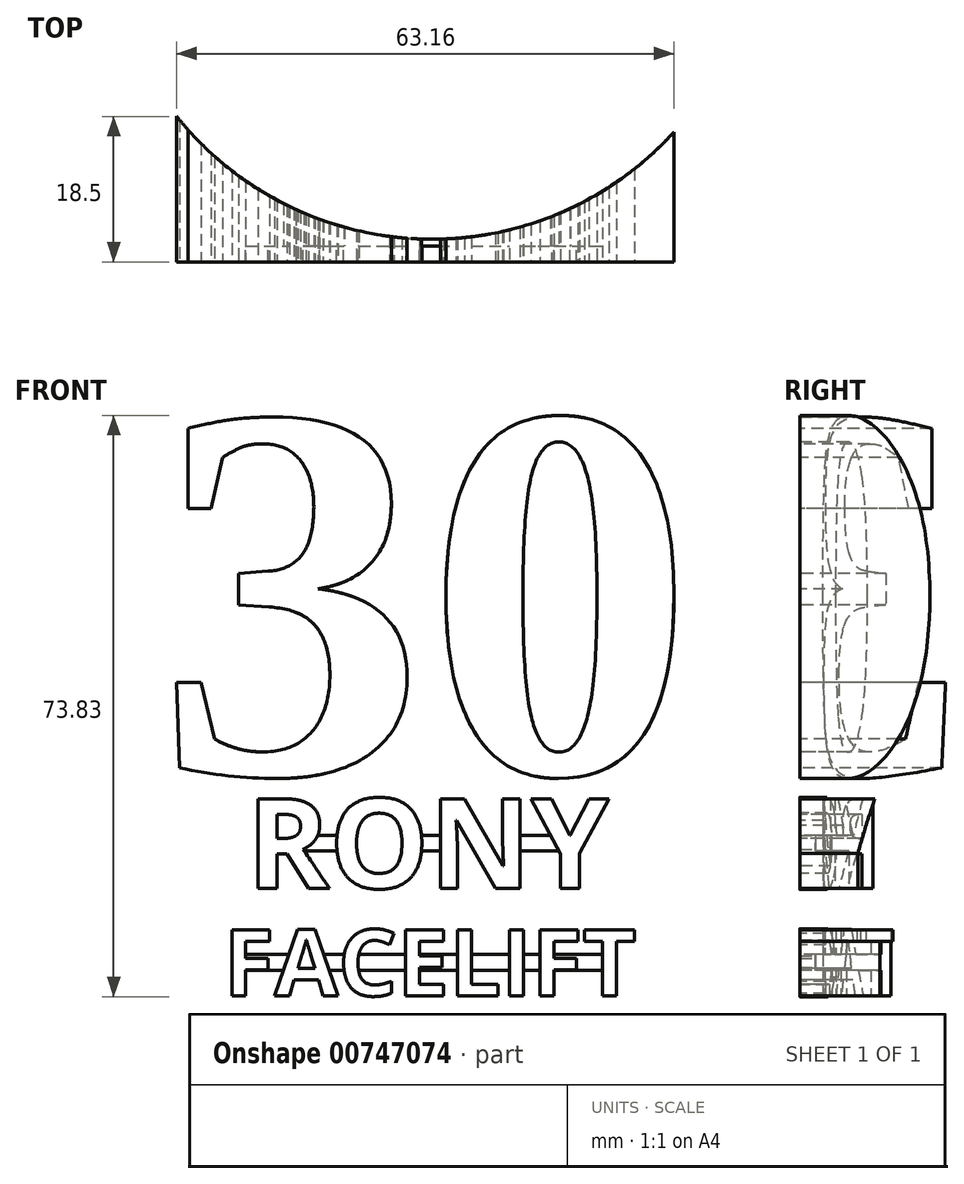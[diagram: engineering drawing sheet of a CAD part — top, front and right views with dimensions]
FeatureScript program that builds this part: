
annotation { "Feature Type Name" : "Feature", "Feature Type Description" : "" }
export const myFeature = defineFeature(function(context is Context, id is Id, definition is map)
    precondition{}
    {
        {
            var Q0;
            Q0=qCreatedBy(makeId("Front.planeOp"),FACE);
            var sketch = newSketch(context, id + "F0", { "sketchPlane" : qUnion([Q0])});
            skText(sketch, "E0", { "text": "30", "fontName": "Tinos-Bold.ttf"});
            skText(sketch, "E1", { "text": "RONY", "fontName": "OpenSans-Bold.ttf"});
            skText(sketch, "E2", { "text": "FACELIFT", "fontName": "OpenSans-Bold.ttf"});
            skLineSegment(sketch, "E3", {"start": v(-23.54, 5.73) * mm, "end": v(23.54, 5.73) * mm});
            skLineSegment(sketch, "E4.0", {"start": v(-23.54, 4.73) * mm, "end": v(23.54, 4.73) * mm});
            skLineSegment(sketch, "E5.MirrorCS", {"start": v(-23.54, 6.73) * mm, "end": v(23.54, 6.73) * mm});
            skLineSegment(sketch, "E6", {"start": v(-26.47, -9.42) * mm, "end": v(26.47, -9.42) * mm});
            skLineSegment(sketch, "E7.0", {"start": v(-26.47, -10.42) * mm, "end": v(26.47, -10.42) * mm});
            skLineSegment(sketch, "E8.MirrorCS", {"start": v(-26.47, -8.42) * mm, "end": v(26.47, -8.42) * mm});
            const initialGuessF0  = {"E0": [-0.035, 0.01461, 1, 0, 0.0492], "E1": [-0.02354, 0, 1, 0, 0.01146], "E2": [-0.02647, -0.01366, 1, 0, 0.00846]};
            skSetInitialGuess(sketch, initialGuessF0);
            skSolve(sketch);
        }
        {
            var Q0;
            Q0=makeQuery(id+"F0.imprint","IMPRINT",FACE,{"disambiguationData":[TD([[makeQuery(id+"F0.imprint","IMPRINT",EDGE,{"derivedFrom":sQuery(id+"F0.wireOp",EDGE,"E0.sketch_text.stroke-0")}),-1.0]])]});
            var Q1;
            Q1=makeQuery(id+"F0.imprint","IMPRINT",FACE,{"disambiguationData":[TD([[makeQuery(id+"F0.imprint","IMPRINT",EDGE,{"derivedFrom":sQuery(id+"F0.wireOp",EDGE,"E0.sketch_text.stroke-29")}),-1.0]])]});
            var Q2;
            Q2=makeQuery(id+"F0.imprint","IMPRINT",FACE,{"disambiguationData":[TD([[makeQuery(id+"F0.imprint","IMPRINT",EDGE,{"derivedFrom":sQuery(id+"F0.wireOp",EDGE,"E1.sketch_text.stroke-7")}),-1.0]])]});
            var Q3;
            {var subQ0=sQuery(id+"F0.wireOp",EDGE,"E1.sketch_text.stroke-38");Q3=makeQuery(id+"F0.imprint","IMPRINT",FACE,{"disambiguationData":[TD([[makeQuery(id+"F0.imprint","IMPRINT",EDGE,{"derivedFrom":subQ0}),-1.0]])]});}
            var Q4;
            {var subQ0=sQuery(id+"F0.wireOp",EDGE,"E1.sketch_text.stroke-45");Q4=makeQuery(id+"F0.imprint","IMPRINT",FACE,{"disambiguationData":[TD([[makeQuery(id+"F0.imprint","IMPRINT",EDGE,{"derivedFrom":subQ0}),-1.0]])]});}
            var Q5;
            {var subQ0=sQuery(id+"F0.wireOp",EDGE,"E1.sketch_text.stroke-55");var subQ1=sQuery(id+"F0.wireOp",EDGE,"E1.sketch_text.stroke-47");var subQ2=makeQuery(id+"F0.imprint","INTERSECT",VERTEX,{"derivedFrom":[subQ1,subQ0]});Q5=makeQuery(id+"F0.imprint","IMPRINT",FACE,{"disambiguationData":[TD([[makeQuery(id+"F0.imprint","IMPRINT",EDGE,{"disambiguationData":[TD([[subQ2,-1.0]])],"derivedFrom":subQ1}),1.0]])]});}
            var Q6;
            {var subQ0=sQuery(id+"F0.wireOp",EDGE,"E1.sketch_text.stroke-48");Q6=makeQuery(id+"F0.imprint","IMPRINT",FACE,{"disambiguationData":[TD([[makeQuery(id+"F0.imprint","IMPRINT",EDGE,{"derivedFrom":subQ0}),-1.0]])]});}
            var Q7;
            {var subQ1=sQuery(id+"F0.wireOp",EDGE,"E1.sketch_text.stroke-50");Q7=makeQuery(id+"F0.imprint","IMPRINT",FACE,{"disambiguationData":[TD([[makeQuery(id+"F0.imprint","IMPRINT",EDGE,{"derivedFrom":subQ1}),-1.0]])]});}
            var Q8;
            {var subQ0=sQuery(id+"F0.wireOp",EDGE,"E1.sketch_text.stroke-54");Q8=makeQuery(id+"F0.imprint","IMPRINT",FACE,{"disambiguationData":[TD([[makeQuery(id+"F0.imprint","IMPRINT",EDGE,{"derivedFrom":subQ0}),-1.0]])]});}
            var Q9;
            {var subQ0=sQuery(id+"F0.wireOp",EDGE,"E2.sketch_text.stroke-0");Q9=makeQuery(id+"F0.imprint","IMPRINT",FACE,{"disambiguationData":[TD([[makeQuery(id+"F0.imprint","IMPRINT",EDGE,{"derivedFrom":subQ0}),-1.0]])]});}
            var Q10;
            {var subQ6=sQuery(id+"F0.wireOp",EDGE,"E2.sketch_text.stroke-2");Q10=makeQuery(id+"F0.imprint","IMPRINT",FACE,{"disambiguationData":[TD([[makeQuery(id+"F0.imprint","IMPRINT",EDGE,{"derivedFrom":subQ6}),-1.0]])]});}
            var Q11;
            Q11=makeQuery(id+"F0.imprint","IMPRINT",FACE,{"disambiguationData":[TD([[makeQuery(id+"F0.imprint","IMPRINT",EDGE,{"derivedFrom":sQuery(id+"F0.wireOp",EDGE,"E2.sketch_text.stroke-10")}),-1.0]])]});
            var Q12;
            {var subQ5=sQuery(id+"F0.wireOp",EDGE,"E2.sketch_text.stroke-22");Q12=makeQuery(id+"F0.imprint","IMPRINT",FACE,{"disambiguationData":[TD([[makeQuery(id+"F0.imprint","IMPRINT",EDGE,{"derivedFrom":subQ5}),-1.0]])]});}
            var Q13;
            {var subQ0=sQuery(id+"F0.wireOp",EDGE,"E2.sketch_text.stroke-25");Q13=makeQuery(id+"F0.imprint","IMPRINT",FACE,{"disambiguationData":[TD([[makeQuery(id+"F0.imprint","IMPRINT",EDGE,{"derivedFrom":subQ0}),-1.0]])]});}
            var Q14;
            {var subQ2=sQuery(id+"F0.wireOp",EDGE,"E2.sketch_text.stroke-37");Q14=makeQuery(id+"F0.imprint","IMPRINT",FACE,{"disambiguationData":[TD([[makeQuery(id+"F0.imprint","IMPRINT",EDGE,{"derivedFrom":subQ2}),-1.0]])]});}
            var Q15;
            {var subQ1=sQuery(id+"F0.wireOp",EDGE,"E2.sketch_text.stroke-39");Q15=makeQuery(id+"F0.imprint","IMPRINT",FACE,{"disambiguationData":[TD([[makeQuery(id+"F0.imprint","IMPRINT",EDGE,{"derivedFrom":subQ1}),-1.0]])]});}
            var Q16;
            {var subQ0=sQuery(id+"F0.wireOp",EDGE,"E2.sketch_text.stroke-52");Q16=makeQuery(id+"F0.imprint","IMPRINT",FACE,{"disambiguationData":[TD([[makeQuery(id+"F0.imprint","IMPRINT",EDGE,{"derivedFrom":subQ0}),-1.0]])]});}
            var Q17;
            {var subQ0=sQuery(id+"F0.wireOp",EDGE,"E2.sketch_text.stroke-50");Q17=makeQuery(id+"F0.imprint","IMPRINT",FACE,{"disambiguationData":[TD([[makeQuery(id+"F0.imprint","IMPRINT",EDGE,{"derivedFrom":subQ0}),-1.0]])]});}
            var Q18;
            {var subQ0=sQuery(id+"F0.wireOp",EDGE,"E2.sketch_text.stroke-58");Q18=makeQuery(id+"F0.imprint","IMPRINT",FACE,{"disambiguationData":[TD([[makeQuery(id+"F0.imprint","IMPRINT",EDGE,{"derivedFrom":subQ0}),-1.0]])]});}
            var Q19;
            {var subQ0=sQuery(id+"F0.wireOp",EDGE,"E2.sketch_text.stroke-56");Q19=makeQuery(id+"F0.imprint","IMPRINT",FACE,{"disambiguationData":[TD([[makeQuery(id+"F0.imprint","IMPRINT",EDGE,{"derivedFrom":subQ0}),-1.0]])]});}
            var Q20;
            {var subQ0=sQuery(id+"F0.wireOp",EDGE,"E2.sketch_text.stroke-59");Q20=makeQuery(id+"F0.imprint","IMPRINT",FACE,{"disambiguationData":[TD([[makeQuery(id+"F0.imprint","IMPRINT",EDGE,{"derivedFrom":subQ0}),-1.0]])]});}
            var Q21;
            {var subQ1=sQuery(id+"F0.wireOp",EDGE,"E2.sketch_text.stroke-61");Q21=makeQuery(id+"F0.imprint","IMPRINT",FACE,{"disambiguationData":[TD([[makeQuery(id+"F0.imprint","IMPRINT",EDGE,{"derivedFrom":subQ1}),-1.0]])]});}
            var Q22;
            {var subQ0=sQuery(id+"F0.wireOp",EDGE,"E2.sketch_text.stroke-69");Q22=makeQuery(id+"F0.imprint","IMPRINT",FACE,{"disambiguationData":[TD([[makeQuery(id+"F0.imprint","IMPRINT",EDGE,{"derivedFrom":subQ0}),-1.0]])]});}
            var Q23;
            {var subQ5=sQuery(id+"F0.wireOp",EDGE,"E2.sketch_text.stroke-71");Q23=makeQuery(id+"F0.imprint","IMPRINT",FACE,{"disambiguationData":[TD([[makeQuery(id+"F0.imprint","IMPRINT",EDGE,{"derivedFrom":subQ5}),-1.0]])]});}
            var Q24;
            {var subQ10=sQuery(id+"F0.wireOp",EDGE,"E1.sketch_text.stroke-3");Q24=makeQuery(id+"F0.imprint","IMPRINT",FACE,{"disambiguationData":[TD([[makeQuery(id+"F0.imprint","IMPRINT",EDGE,{"derivedFrom":subQ10}),-1.0]])]});}
            var Q25;
            {var subQ1=sQuery(id+"F0.wireOp",EDGE,"E1.sketch_text.stroke-9");var subQ7=sQuery(id+"F0.wireOp",EDGE,"E4.0");var subQ9=makeQuery(id+"F0.imprint","INTERSECT",VERTEX,{"derivedFrom":[subQ1,subQ7]});Q25=makeQuery(id+"F0.imprint","IMPRINT",FACE,{"disambiguationData":[TD([[makeQuery(id+"F0.imprint","IMPRINT",EDGE,{"disambiguationData":[TD([[subQ9,-1.0]])],"derivedFrom":subQ1}),-1.0]])]});}
            var Q26;
            {var subQ1=sQuery(id+"F0.wireOp",EDGE,"E1.sketch_text.stroke-14");var subQ7=sQuery(id+"F0.wireOp",EDGE,"E1.sketch_text.stroke-13");var subQ8=makeQuery(id+"F0.imprint","INTERSECT",VERTEX,{"derivedFrom":[subQ7,subQ1]});Q26=makeQuery(id+"F0.imprint","IMPRINT",FACE,{"disambiguationData":[TD([[makeQuery(id+"F0.imprint","IMPRINT",EDGE,{"disambiguationData":[TD([[subQ8,1.0]])],"derivedFrom":subQ7}),1.0]])]});}
            var Q27;
            {var subQ5=sQuery(id+"F0.wireOp",EDGE,"E1.sketch_text.stroke-15");var subQ6=sQuery(id+"F0.wireOp",EDGE,"E1.sketch_text.stroke-14");var subQ7=makeQuery(id+"F0.imprint","INTERSECT",VERTEX,{"derivedFrom":[subQ6,subQ5]});Q27=makeQuery(id+"F0.imprint","IMPRINT",FACE,{"disambiguationData":[TD([[makeQuery(id+"F0.imprint","IMPRINT",EDGE,{"disambiguationData":[TD([[subQ7,1.0]])],"derivedFrom":subQ6}),1.0]])]});}
            var Q28;
            {var subQ1=sQuery(id+"F0.wireOp",EDGE,"E1.sketch_text.stroke-26");var subQ5=sQuery(id+"F0.wireOp",EDGE,"E1.sketch_text.stroke-19");var subQ6=makeQuery(id+"F0.imprint","INTERSECT",VERTEX,{"derivedFrom":[subQ5,subQ1]});Q28=makeQuery(id+"F0.imprint","IMPRINT",FACE,{"disambiguationData":[TD([[makeQuery(id+"F0.imprint","IMPRINT",EDGE,{"disambiguationData":[TD([[subQ6,-1.0]])],"derivedFrom":subQ5}),1.0]])]});}
            var Q29;
            {var subQ7=sQuery(id+"F0.wireOp",EDGE,"E1.sketch_text.stroke-20");Q29=makeQuery(id+"F0.imprint","IMPRINT",FACE,{"disambiguationData":[TD([[makeQuery(id+"F0.imprint","IMPRINT",EDGE,{"derivedFrom":subQ7}),-1.0]])]});}
            var Q30;
            {var subQ7=sQuery(id+"F0.wireOp",EDGE,"E1.sketch_text.stroke-24");Q30=makeQuery(id+"F0.imprint","IMPRINT",FACE,{"disambiguationData":[TD([[makeQuery(id+"F0.imprint","IMPRINT",EDGE,{"derivedFrom":subQ7}),-1.0]])]});}
            var Q31;
            {var subQ0=sQuery(id+"F0.wireOp",EDGE,"E5.MirrorCS");var subQ1=sQuery(id+"F0.wireOp",EDGE,"E1.sketch_text.stroke-26");var subQ2=makeQuery(id+"F0.imprint","INTERSECT",VERTEX,{"derivedFrom":[subQ1,subQ0]});Q31=makeQuery(id+"F0.imprint","IMPRINT",FACE,{"disambiguationData":[TD([[makeQuery(id+"F0.imprint","IMPRINT",EDGE,{"disambiguationData":[TD([[subQ2,-1.0]])],"derivedFrom":subQ1}),1.0]])]});}
            var Q32;
            {var subQ2=sQuery(id+"F0.wireOp",EDGE,"E1.sketch_text.stroke-33");Q32=makeQuery(id+"F0.imprint","IMPRINT",FACE,{"disambiguationData":[TD([[makeQuery(id+"F0.imprint","IMPRINT",EDGE,{"derivedFrom":subQ2}),-1.0]])]});}
            var Q33;
            {var subQ1=sQuery(id+"F0.wireOp",EDGE,"E1.sketch_text.stroke-35");Q33=makeQuery(id+"F0.imprint","IMPRINT",FACE,{"disambiguationData":[TD([[makeQuery(id+"F0.imprint","IMPRINT",EDGE,{"derivedFrom":subQ1}),-1.0]])]});}
            var Q34;
            {var subQ0=sQuery(id+"F0.wireOp",EDGE,"E5.MirrorCS");var subQ1=sQuery(id+"F0.wireOp",EDGE,"E1.sketch_text.stroke-46");var subQ2=makeQuery(id+"F0.imprint","INTERSECT",VERTEX,{"derivedFrom":[subQ1,subQ0]});Q34=makeQuery(id+"F0.imprint","IMPRINT",FACE,{"disambiguationData":[TD([[makeQuery(id+"F0.imprint","IMPRINT",EDGE,{"disambiguationData":[TD([[subQ2,-1.0]])],"derivedFrom":subQ1}),1.0]])]});}
            var Q35;
            {var subQ0=sQuery(id+"F0.wireOp",EDGE,"E4.0");var subQ1=sQuery(id+"F0.wireOp",EDGE,"E1.sketch_text.stroke-46");var subQ2=makeQuery(id+"F0.imprint","INTERSECT",VERTEX,{"derivedFrom":[subQ1,subQ0]});Q35=makeQuery(id+"F0.imprint","IMPRINT",FACE,{"disambiguationData":[TD([[makeQuery(id+"F0.imprint","IMPRINT",EDGE,{"disambiguationData":[TD([[subQ2,1.0]])],"derivedFrom":subQ1}),1.0]])]});}
            var Q36;
            {var subQ0=sQuery(id+"F0.wireOp",EDGE,"E3");var subQ1=sQuery(id+"F0.wireOp",EDGE,"E1.sketch_text.stroke-49");var subQ2=makeQuery(id+"F0.imprint","INTERSECT",VERTEX,{"derivedFrom":[subQ1,subQ0]});Q36=makeQuery(id+"F0.imprint","IMPRINT",FACE,{"disambiguationData":[TD([[makeQuery(id+"F0.imprint","IMPRINT",EDGE,{"disambiguationData":[TD([[subQ2,-1.0]])],"derivedFrom":subQ1}),-1.0]])]});}
            var Q37;
            {var subQ1=sQuery(id+"F0.wireOp",EDGE,"E2.sketch_text.stroke-8");Q37=makeQuery(id+"F0.imprint","IMPRINT",FACE,{"disambiguationData":[TD([[makeQuery(id+"F0.imprint","IMPRINT",EDGE,{"derivedFrom":subQ1}),-1.0]])]});}
            var Q38;
            {var subQ1=sQuery(id+"F0.wireOp",EDGE,"E2.sketch_text.stroke-6");Q38=makeQuery(id+"F0.imprint","IMPRINT",FACE,{"disambiguationData":[TD([[makeQuery(id+"F0.imprint","IMPRINT",EDGE,{"derivedFrom":subQ1}),-1.0]])]});}
            var Q39;
            {var subQ6=sQuery(id+"F0.wireOp",EDGE,"E2.sketch_text.stroke-6");Q39=makeQuery(id+"F0.imprint","IMPRINT",FACE,{"disambiguationData":[TD([[makeQuery(id+"F0.imprint","IMPRINT",EDGE,{"derivedFrom":subQ6}),1.0]])]});}
            var Q40;
            {var subQ6=sQuery(id+"F0.wireOp",EDGE,"E2.sketch_text.stroke-8");Q40=makeQuery(id+"F0.imprint","IMPRINT",FACE,{"disambiguationData":[TD([[makeQuery(id+"F0.imprint","IMPRINT",EDGE,{"derivedFrom":subQ6}),1.0]])]});}
            var Q41;
            {var subQ6=sQuery(id+"F0.wireOp",EDGE,"E2.sketch_text.stroke-15");Q41=makeQuery(id+"F0.imprint","IMPRINT",FACE,{"disambiguationData":[TD([[makeQuery(id+"F0.imprint","IMPRINT",EDGE,{"derivedFrom":subQ6}),-1.0]])]});}
            var Q42;
            {var subQ0=sQuery(id+"F0.wireOp",EDGE,"E8.MirrorCS");var subQ1=sQuery(id+"F0.wireOp",EDGE,"E2.sketch_text.stroke-16");var subQ2=makeQuery(id+"F0.imprint","INTERSECT",VERTEX,{"derivedFrom":[subQ1,subQ0]});Q42=makeQuery(id+"F0.imprint","IMPRINT",FACE,{"disambiguationData":[TD([[makeQuery(id+"F0.imprint","IMPRINT",EDGE,{"disambiguationData":[TD([[subQ2,-1.0]])],"derivedFrom":subQ1}),1.0]])]});}
            var Q43;
            {var subQ5=sQuery(id+"F0.wireOp",EDGE,"E7.0");var subQ7=sQuery(id+"F0.wireOp",EDGE,"E2.sketch_text.stroke-16");var subQ8=makeQuery(id+"F0.imprint","INTERSECT",VERTEX,{"derivedFrom":[subQ7,subQ5]});Q43=makeQuery(id+"F0.imprint","IMPRINT",FACE,{"disambiguationData":[TD([[makeQuery(id+"F0.imprint","IMPRINT",EDGE,{"disambiguationData":[TD([[subQ8,1.0]])],"derivedFrom":subQ7}),1.0]])]});}
            var Q44;
            {var subQ0=sQuery(id+"F0.wireOp",EDGE,"E8.MirrorCS");var subQ1=sQuery(id+"F0.wireOp",EDGE,"E2.sketch_text.stroke-23");var subQ2=makeQuery(id+"F0.imprint","INTERSECT",VERTEX,{"derivedFrom":[subQ1,subQ0]});Q44=makeQuery(id+"F0.imprint","IMPRINT",FACE,{"disambiguationData":[TD([[makeQuery(id+"F0.imprint","IMPRINT",EDGE,{"disambiguationData":[TD([[subQ2,-1.0]])],"derivedFrom":subQ1}),1.0]])]});}
            var Q45;
            {var subQ1=sQuery(id+"F0.wireOp",EDGE,"E2.sketch_text.stroke-23");var subQ5=sQuery(id+"F0.wireOp",EDGE,"E2.sketch_text.stroke-24");var subQ6=makeQuery(id+"F0.imprint","INTERSECT",VERTEX,{"derivedFrom":[subQ1,subQ5]});Q45=makeQuery(id+"F0.imprint","IMPRINT",FACE,{"disambiguationData":[TD([[makeQuery(id+"F0.imprint","IMPRINT",EDGE,{"disambiguationData":[TD([[subQ6,1.0]])],"derivedFrom":subQ1}),1.0]])]});}
            var Q46;
            {var subQ1=sQuery(id+"F0.wireOp",EDGE,"E2.sketch_text.stroke-43");Q46=makeQuery(id+"F0.imprint","IMPRINT",FACE,{"disambiguationData":[TD([[makeQuery(id+"F0.imprint","IMPRINT",EDGE,{"derivedFrom":subQ1}),1.0]])]});}
            var Q47;
            {var subQ6=sQuery(id+"F0.wireOp",EDGE,"E2.sketch_text.stroke-45");Q47=makeQuery(id+"F0.imprint","IMPRINT",FACE,{"disambiguationData":[TD([[makeQuery(id+"F0.imprint","IMPRINT",EDGE,{"derivedFrom":subQ6}),1.0]])]});}
            var Q48;
            {var subQ0=sQuery(id+"F0.wireOp",EDGE,"E8.MirrorCS");var subQ1=sQuery(id+"F0.wireOp",EDGE,"E2.sketch_text.stroke-51");var subQ2=makeQuery(id+"F0.imprint","INTERSECT",VERTEX,{"derivedFrom":[subQ1,subQ0]});Q48=makeQuery(id+"F0.imprint","IMPRINT",FACE,{"disambiguationData":[TD([[makeQuery(id+"F0.imprint","IMPRINT",EDGE,{"disambiguationData":[TD([[subQ2,-1.0]])],"derivedFrom":subQ1}),1.0]])]});}
            var Q49;
            {var subQ0=sQuery(id+"F0.wireOp",EDGE,"E7.0");var subQ1=sQuery(id+"F0.wireOp",EDGE,"E2.sketch_text.stroke-51");var subQ2=makeQuery(id+"F0.imprint","INTERSECT",VERTEX,{"derivedFrom":[subQ1,subQ0]});Q49=makeQuery(id+"F0.imprint","IMPRINT",FACE,{"disambiguationData":[TD([[makeQuery(id+"F0.imprint","IMPRINT",EDGE,{"disambiguationData":[TD([[subQ2,1.0]])],"derivedFrom":subQ1}),1.0]])]});}
            var Q50;
            {var subQ0=sQuery(id+"F0.wireOp",EDGE,"E8.MirrorCS");var subQ1=sQuery(id+"F0.wireOp",EDGE,"E2.sketch_text.stroke-57");var subQ2=makeQuery(id+"F0.imprint","INTERSECT",VERTEX,{"derivedFrom":[subQ1,subQ0]});Q50=makeQuery(id+"F0.imprint","IMPRINT",FACE,{"disambiguationData":[TD([[makeQuery(id+"F0.imprint","IMPRINT",EDGE,{"disambiguationData":[TD([[subQ2,-1.0]])],"derivedFrom":subQ1}),1.0]])]});}
            var Q51;
            {var subQ0=sQuery(id+"F0.wireOp",EDGE,"E7.0");var subQ1=sQuery(id+"F0.wireOp",EDGE,"E2.sketch_text.stroke-57");var subQ2=makeQuery(id+"F0.imprint","INTERSECT",VERTEX,{"derivedFrom":[subQ1,subQ0]});Q51=makeQuery(id+"F0.imprint","IMPRINT",FACE,{"disambiguationData":[TD([[makeQuery(id+"F0.imprint","IMPRINT",EDGE,{"disambiguationData":[TD([[subQ2,1.0]])],"derivedFrom":subQ1}),1.0]])]});}
            var Q52;
            {var subQ1=sQuery(id+"F0.wireOp",EDGE,"E2.sketch_text.stroke-65");Q52=makeQuery(id+"F0.imprint","IMPRINT",FACE,{"disambiguationData":[TD([[makeQuery(id+"F0.imprint","IMPRINT",EDGE,{"derivedFrom":subQ1}),1.0]])]});}
            var Q53;
            {var subQ1=sQuery(id+"F0.wireOp",EDGE,"E2.sketch_text.stroke-67");Q53=makeQuery(id+"F0.imprint","IMPRINT",FACE,{"disambiguationData":[TD([[makeQuery(id+"F0.imprint","IMPRINT",EDGE,{"derivedFrom":subQ1}),1.0]])]});}
            var Q54;
            {var subQ0=sQuery(id+"F0.wireOp",EDGE,"E7.0");var subQ1=sQuery(id+"F0.wireOp",EDGE,"E2.sketch_text.stroke-70");var subQ2=makeQuery(id+"F0.imprint","INTERSECT",VERTEX,{"derivedFrom":[subQ1,subQ0]});Q54=makeQuery(id+"F0.imprint","IMPRINT",FACE,{"disambiguationData":[TD([[makeQuery(id+"F0.imprint","IMPRINT",EDGE,{"disambiguationData":[TD([[subQ2,-1.0]])],"derivedFrom":subQ1}),-1.0]])]});}
            var Q55;
            {var subQ0=sQuery(id+"F0.wireOp",EDGE,"E8.MirrorCS");var subQ1=sQuery(id+"F0.wireOp",EDGE,"E2.sketch_text.stroke-70");var subQ2=makeQuery(id+"F0.imprint","INTERSECT",VERTEX,{"derivedFrom":[subQ1,subQ0]});Q55=makeQuery(id+"F0.imprint","IMPRINT",FACE,{"disambiguationData":[TD([[makeQuery(id+"F0.imprint","IMPRINT",EDGE,{"disambiguationData":[TD([[subQ2,1.0]])],"derivedFrom":subQ1}),-1.0]])]});}
            var Q56;
            {var subQ1=sQuery(id+"F0.wireOp",EDGE,"E1.sketch_text.stroke-0");Q56=makeQuery(id+"F0.imprint","IMPRINT",FACE,{"disambiguationData":[TD([[makeQuery(id+"F0.imprint","IMPRINT",EDGE,{"derivedFrom":subQ1}),-1.0]])]});}
            var Q57;
            {var subQ7=sQuery(id+"F0.wireOp",EDGE,"E1.sketch_text.stroke-26");var subQ8=sQuery(id+"F0.wireOp",EDGE,"E1.sketch_text.stroke-19");var subQ9=makeQuery(id+"F0.imprint","INTERSECT",VERTEX,{"derivedFrom":[subQ8,subQ7]});Q57=makeQuery(id+"F0.imprint","IMPRINT",FACE,{"disambiguationData":[TD([[makeQuery(id+"F0.imprint","IMPRINT",EDGE,{"disambiguationData":[TD([[subQ9,-1.0]])],"derivedFrom":subQ8}),-1.0]])]});}
            var Q58;
            {var subQ7=sQuery(id+"F0.wireOp",EDGE,"E1.sketch_text.stroke-23");var subQ8=sQuery(id+"F0.wireOp",EDGE,"E1.sketch_text.stroke-22");var subQ9=makeQuery(id+"F0.imprint","INTERSECT",VERTEX,{"derivedFrom":[subQ8,subQ7]});Q58=makeQuery(id+"F0.imprint","IMPRINT",FACE,{"disambiguationData":[TD([[makeQuery(id+"F0.imprint","IMPRINT",EDGE,{"disambiguationData":[TD([[subQ9,1.0]])],"derivedFrom":subQ8}),-1.0]])]});}
            var Q59;
            {var subQ0=sQuery(id+"F0.wireOp",EDGE,"E5.MirrorCS");var subQ1=sQuery(id+"F0.wireOp",EDGE,"E1.sketch_text.stroke-23");var subQ2=makeQuery(id+"F0.imprint","INTERSECT",VERTEX,{"derivedFrom":[subQ1,subQ0]});Q59=makeQuery(id+"F0.imprint","IMPRINT",FACE,{"disambiguationData":[TD([[makeQuery(id+"F0.imprint","IMPRINT",EDGE,{"disambiguationData":[TD([[subQ2,1.0]])],"derivedFrom":subQ1}),-1.0]])]});}
            var Q60;
            {var subQ0=sQuery(id+"F0.wireOp",EDGE,"E5.MirrorCS");var subQ1=sQuery(id+"F0.wireOp",EDGE,"E1.sketch_text.stroke-26");var subQ2=makeQuery(id+"F0.imprint","INTERSECT",VERTEX,{"derivedFrom":[subQ1,subQ0]});Q60=makeQuery(id+"F0.imprint","IMPRINT",FACE,{"disambiguationData":[TD([[makeQuery(id+"F0.imprint","IMPRINT",EDGE,{"disambiguationData":[TD([[subQ2,-1.0]])],"derivedFrom":subQ1}),-1.0]])]});}
            var Q61;
            {var subQ0=sQuery(id+"F0.wireOp",EDGE,"E4.0");var subQ1=sQuery(id+"F0.wireOp",EDGE,"E1.sketch_text.stroke-34");var subQ2=makeQuery(id+"F0.imprint","INTERSECT",VERTEX,{"derivedFrom":[subQ1,subQ0]});Q61=makeQuery(id+"F0.imprint","IMPRINT",FACE,{"disambiguationData":[TD([[makeQuery(id+"F0.imprint","IMPRINT",EDGE,{"disambiguationData":[TD([[subQ2,-1.0]])],"derivedFrom":subQ1}),-1.0]])]});}
            var Q62;
            {var subQ0=sQuery(id+"F0.wireOp",EDGE,"E3");var subQ1=sQuery(id+"F0.wireOp",EDGE,"E1.sketch_text.stroke-34");var subQ2=makeQuery(id+"F0.imprint","INTERSECT",VERTEX,{"derivedFrom":[subQ1,subQ0]});Q62=makeQuery(id+"F0.imprint","IMPRINT",FACE,{"disambiguationData":[TD([[makeQuery(id+"F0.imprint","IMPRINT",EDGE,{"disambiguationData":[TD([[subQ2,-1.0]])],"derivedFrom":subQ1}),-1.0]])]});}
            var Q63;
            {var subQ0=sQuery(id+"F0.wireOp",EDGE,"E5.MirrorCS");var subQ1=sQuery(id+"F0.wireOp",EDGE,"E1.sketch_text.stroke-36");var subQ2=makeQuery(id+"F0.imprint","INTERSECT",VERTEX,{"derivedFrom":[subQ1,subQ0]});Q63=makeQuery(id+"F0.imprint","IMPRINT",FACE,{"disambiguationData":[TD([[makeQuery(id+"F0.imprint","IMPRINT",EDGE,{"disambiguationData":[TD([[subQ2,-1.0]])],"derivedFrom":subQ1}),-1.0]])]});}
            var Q64;
            {var subQ1=sQuery(id+"F0.wireOp",EDGE,"E1.sketch_text.stroke-36");var subQ5=sQuery(id+"F0.wireOp",EDGE,"E1.sketch_text.stroke-37");var subQ6=makeQuery(id+"F0.imprint","INTERSECT",VERTEX,{"derivedFrom":[subQ1,subQ5]});Q64=makeQuery(id+"F0.imprint","IMPRINT",FACE,{"disambiguationData":[TD([[makeQuery(id+"F0.imprint","IMPRINT",EDGE,{"disambiguationData":[TD([[subQ6,1.0]])],"derivedFrom":subQ1}),-1.0]])]});}
            var Q65;
            {var subQ0=sQuery(id+"F0.wireOp",EDGE,"E4.0");var subQ1=sQuery(id+"F0.wireOp",EDGE,"E1.sketch_text.stroke-43");var subQ2=makeQuery(id+"F0.imprint","INTERSECT",VERTEX,{"derivedFrom":[subQ1,subQ0]});Q65=makeQuery(id+"F0.imprint","IMPRINT",FACE,{"disambiguationData":[TD([[makeQuery(id+"F0.imprint","IMPRINT",EDGE,{"disambiguationData":[TD([[subQ2,-1.0]])],"derivedFrom":subQ1}),-1.0]])]});}
            var Q66;
            {var subQ1=sQuery(id+"F0.wireOp",EDGE,"E1.sketch_text.stroke-43");var subQ5=sQuery(id+"F0.wireOp",EDGE,"E1.sketch_text.stroke-44");var subQ6=makeQuery(id+"F0.imprint","INTERSECT",VERTEX,{"derivedFrom":[subQ1,subQ5]});Q66=makeQuery(id+"F0.imprint","IMPRINT",FACE,{"disambiguationData":[TD([[makeQuery(id+"F0.imprint","IMPRINT",EDGE,{"disambiguationData":[TD([[subQ6,1.0]])],"derivedFrom":subQ1}),-1.0]])]});}
            var Q67;
            {var subQ0=sQuery(id+"F0.wireOp",EDGE,"E8.MirrorCS");var subQ1=sQuery(id+"F0.wireOp",EDGE,"E2.sketch_text.stroke-14");var subQ2=makeQuery(id+"F0.imprint","INTERSECT",VERTEX,{"derivedFrom":[subQ1,subQ0]});Q67=makeQuery(id+"F0.imprint","IMPRINT",FACE,{"disambiguationData":[TD([[makeQuery(id+"F0.imprint","IMPRINT",EDGE,{"disambiguationData":[TD([[subQ2,1.0]])],"derivedFrom":subQ1}),-1.0]])]});}
            var Q68;
            {var subQ0=sQuery(id+"F0.wireOp",EDGE,"E8.MirrorCS");var subQ1=sQuery(id+"F0.wireOp",EDGE,"E2.sketch_text.stroke-16");var subQ2=makeQuery(id+"F0.imprint","INTERSECT",VERTEX,{"derivedFrom":[subQ1,subQ0]});Q68=makeQuery(id+"F0.imprint","IMPRINT",FACE,{"disambiguationData":[TD([[makeQuery(id+"F0.imprint","IMPRINT",EDGE,{"disambiguationData":[TD([[subQ2,-1.0]])],"derivedFrom":subQ1}),-1.0]])]});}
            var Q69;
            {var subQ0=sQuery(id+"F0.wireOp",EDGE,"E8.MirrorCS");var subQ1=sQuery(id+"F0.wireOp",EDGE,"E2.sketch_text.stroke-23");var subQ2=makeQuery(id+"F0.imprint","INTERSECT",VERTEX,{"derivedFrom":[subQ1,subQ0]});Q69=makeQuery(id+"F0.imprint","IMPRINT",FACE,{"disambiguationData":[TD([[makeQuery(id+"F0.imprint","IMPRINT",EDGE,{"disambiguationData":[TD([[subQ2,-1.0]])],"derivedFrom":subQ1}),-1.0]])]});}
            var Q70;
            {var subQ6=sQuery(id+"F0.wireOp",EDGE,"E2.sketch_text.stroke-24");var subQ9=sQuery(id+"F0.wireOp",EDGE,"E2.sketch_text.stroke-23");var subQ10=makeQuery(id+"F0.imprint","INTERSECT",VERTEX,{"derivedFrom":[subQ9,subQ6]});Q70=makeQuery(id+"F0.imprint","IMPRINT",FACE,{"disambiguationData":[TD([[makeQuery(id+"F0.imprint","IMPRINT",EDGE,{"disambiguationData":[TD([[subQ10,1.0]])],"derivedFrom":subQ9}),-1.0]])]});}
            var Q71;
            {var subQ1=sQuery(id+"F0.wireOp",EDGE,"E2.sketch_text.stroke-45");Q71=makeQuery(id+"F0.imprint","IMPRINT",FACE,{"disambiguationData":[TD([[makeQuery(id+"F0.imprint","IMPRINT",EDGE,{"derivedFrom":subQ1}),-1.0]])]});}
            var Q72;
            {var subQ1=sQuery(id+"F0.wireOp",EDGE,"E2.sketch_text.stroke-43");Q72=makeQuery(id+"F0.imprint","IMPRINT",FACE,{"disambiguationData":[TD([[makeQuery(id+"F0.imprint","IMPRINT",EDGE,{"derivedFrom":subQ1}),-1.0]])]});}
            var Q73;
            {var subQ0=sQuery(id+"F0.wireOp",EDGE,"E7.0");var subQ1=sQuery(id+"F0.wireOp",EDGE,"E2.sketch_text.stroke-49");var subQ2=makeQuery(id+"F0.imprint","INTERSECT",VERTEX,{"derivedFrom":[subQ1,subQ0]});Q73=makeQuery(id+"F0.imprint","IMPRINT",FACE,{"disambiguationData":[TD([[makeQuery(id+"F0.imprint","IMPRINT",EDGE,{"disambiguationData":[TD([[subQ2,-1.0]])],"derivedFrom":subQ1}),-1.0]])]});}
            var Q74;
            {var subQ0=sQuery(id+"F0.wireOp",EDGE,"E8.MirrorCS");var subQ1=sQuery(id+"F0.wireOp",EDGE,"E2.sketch_text.stroke-49");var subQ2=makeQuery(id+"F0.imprint","INTERSECT",VERTEX,{"derivedFrom":[subQ1,subQ0]});Q74=makeQuery(id+"F0.imprint","IMPRINT",FACE,{"disambiguationData":[TD([[makeQuery(id+"F0.imprint","IMPRINT",EDGE,{"disambiguationData":[TD([[subQ2,1.0]])],"derivedFrom":subQ1}),-1.0]])]});}
            var Q75;
            {var subQ0=sQuery(id+"F0.wireOp",EDGE,"E7.0");var subQ1=sQuery(id+"F0.wireOp",EDGE,"E2.sketch_text.stroke-55");var subQ2=makeQuery(id+"F0.imprint","INTERSECT",VERTEX,{"derivedFrom":[subQ1,subQ0]});Q75=makeQuery(id+"F0.imprint","IMPRINT",FACE,{"disambiguationData":[TD([[makeQuery(id+"F0.imprint","IMPRINT",EDGE,{"disambiguationData":[TD([[subQ2,-1.0]])],"derivedFrom":subQ1}),-1.0]])]});}
            var Q76;
            {var subQ0=sQuery(id+"F0.wireOp",EDGE,"E8.MirrorCS");var subQ1=sQuery(id+"F0.wireOp",EDGE,"E2.sketch_text.stroke-55");var subQ2=makeQuery(id+"F0.imprint","INTERSECT",VERTEX,{"derivedFrom":[subQ1,subQ0]});Q76=makeQuery(id+"F0.imprint","IMPRINT",FACE,{"disambiguationData":[TD([[makeQuery(id+"F0.imprint","IMPRINT",EDGE,{"disambiguationData":[TD([[subQ2,1.0]])],"derivedFrom":subQ1}),-1.0]])]});}
            var Q77;
            {var subQ1=sQuery(id+"F0.wireOp",EDGE,"E2.sketch_text.stroke-67");Q77=makeQuery(id+"F0.imprint","IMPRINT",FACE,{"disambiguationData":[TD([[makeQuery(id+"F0.imprint","IMPRINT",EDGE,{"derivedFrom":subQ1}),-1.0]])]});}
            var Q78;
            {var subQ1=sQuery(id+"F0.wireOp",EDGE,"E2.sketch_text.stroke-65");Q78=makeQuery(id+"F0.imprint","IMPRINT",FACE,{"disambiguationData":[TD([[makeQuery(id+"F0.imprint","IMPRINT",EDGE,{"derivedFrom":subQ1}),-1.0]])]});}
            var Q79;
            {var subQ0=sQuery(id+"F0.wireOp",EDGE,"E1.sketch_text.stroke-55");var subQ1=sQuery(id+"F0.wireOp",EDGE,"E1.sketch_text.stroke-47");var subQ2=makeQuery(id+"F0.imprint","INTERSECT",VERTEX,{"derivedFrom":[subQ1,subQ0]});Q79=makeQuery(id+"F0.imprint","IMPRINT",FACE,{"disambiguationData":[TD([[makeQuery(id+"F0.imprint","IMPRINT",EDGE,{"disambiguationData":[TD([[subQ2,-1.0]])],"derivedFrom":subQ1}),-1.0]])]});}
            var Q80;
            {var subQ0=sQuery(id+"F0.wireOp",EDGE,"E2.sketch_text.stroke-21");Q80=makeQuery(id+"F0.imprint","IMPRINT",FACE,{"disambiguationData":[TD([[makeQuery(id+"F0.imprint","IMPRINT",EDGE,{"derivedFrom":subQ0}),-1.0]])]});}
            extrude(context, id + "F1", {"entities" : qUnion([Q0, Q1, Q2, Q3, Q4, Q5, Q6, Q7, Q8, Q9, Q10, Q11, Q12, Q13, Q14, Q15, Q16, Q17, Q18, Q19, Q20, Q21, Q22, Q23, Q24, Q25, Q26, Q27, Q28, Q29, Q30, Q31, Q32, Q33, Q34, Q35, Q36, Q37, Q38, Q39, Q40, Q41, Q42, Q43, Q44, Q45, Q46, Q47, Q48, Q49, Q50, Q51, Q52, Q53, Q54, Q55, Q56, Q57, Q58, Q59, Q60, Q61, Q62, Q63, Q64, Q65, Q66, Q67, Q68, Q69, Q70, Q71, Q72, Q73, Q74, Q75, Q76, Q77, Q78, Q79, Q80]), "oppositeDirection" : true, "depth" : 30 * mm, "offsetDistance" : 25 * mm});
        }
        {
            var Q0;
            Q0=qCreatedBy(makeId("Top.planeOp"),FACE);
            var sketch = newSketch(context, id + "F2", { "sketchPlane" : qUnion([Q0])});
            skCircle(sketch, "E9", {"center": v(0, 0) * mm, "radius": 41.5 * mm});
            skSolve(sketch);
        }
        {
            var Q0;
            Q0=makeQuery(id+"F2.imprint","IMPRINT",FACE,{"disambiguationData":[TD([[makeQuery(id+"F2.imprint","IMPRINT",EDGE,{"derivedFrom":sQuery(id+"F2.wireOp",EDGE,"E9")}),1.0]])]});
            extrude(context, id + "F3", {"entities" : qUnion([Q0]), "endBound" : BoundingType.SYMMETRIC, "depth" : 200 * mm, "offsetDistance" : 25 * mm});
        }
        {
            var Q0;
            Q0=makeQuery(id+"F3.opExtrude","SWEPT_BODY",BODY,{"disambiguationData":[OSD([sQuery(id+"F2.wireOp",EDGE,"E9")])]});
            transform(context, id + "F4", {"entities" : qUnion([Q0]), "transformType" : TransformType.TRANSLATION_3D, "dx" : 0 * mm, "dy" : 42.4 * mm, "dz" : 0 * mm, "makeCopy" : false});
        }
        {
            var Q0;
            Q0=makeQuery(id+"F0.imprint","IMPRINT",FACE,{"disambiguationData":[TD([[makeQuery(id+"F0.imprint","IMPRINT",EDGE,{"derivedFrom":sQuery(id+"F0.wireOp",EDGE,"E0.sketch_text.stroke-0")}),-1.0]])]});
            var Q1;
            Q1=makeQuery(id+"F0.imprint","IMPRINT",FACE,{"disambiguationData":[TD([[makeQuery(id+"F0.imprint","IMPRINT",EDGE,{"derivedFrom":sQuery(id+"F0.wireOp",EDGE,"E0.sketch_text.stroke-29")}),-1.0]])]});
            var Q2;
            Q2=makeQuery(id+"F0.imprint","IMPRINT",FACE,{"disambiguationData":[TD([[makeQuery(id+"F0.imprint","IMPRINT",EDGE,{"derivedFrom":sQuery(id+"F0.wireOp",EDGE,"E1.sketch_text.stroke-7")}),-1.0]])]});
            var Q3;
            {var subQ1=sQuery(id+"F0.wireOp",EDGE,"E1.sketch_text.stroke-0");Q3=makeQuery(id+"F0.imprint","IMPRINT",FACE,{"disambiguationData":[TD([[makeQuery(id+"F0.imprint","IMPRINT",EDGE,{"derivedFrom":subQ1}),-1.0]])]});}
            var Q4;
            {var subQ1=sQuery(id+"F0.wireOp",EDGE,"E1.sketch_text.stroke-9");var subQ7=sQuery(id+"F0.wireOp",EDGE,"E4.0");var subQ9=makeQuery(id+"F0.imprint","INTERSECT",VERTEX,{"derivedFrom":[subQ1,subQ7]});Q4=makeQuery(id+"F0.imprint","IMPRINT",FACE,{"disambiguationData":[TD([[makeQuery(id+"F0.imprint","IMPRINT",EDGE,{"disambiguationData":[TD([[subQ9,-1.0]])],"derivedFrom":subQ1}),-1.0]])]});}
            var Q5;
            {var subQ10=sQuery(id+"F0.wireOp",EDGE,"E1.sketch_text.stroke-3");Q5=makeQuery(id+"F0.imprint","IMPRINT",FACE,{"disambiguationData":[TD([[makeQuery(id+"F0.imprint","IMPRINT",EDGE,{"derivedFrom":subQ10}),-1.0]])]});}
            var Q6;
            {var subQ7=sQuery(id+"F0.wireOp",EDGE,"E1.sketch_text.stroke-24");Q6=makeQuery(id+"F0.imprint","IMPRINT",FACE,{"disambiguationData":[TD([[makeQuery(id+"F0.imprint","IMPRINT",EDGE,{"derivedFrom":subQ7}),-1.0]])]});}
            var Q7;
            {var subQ0=sQuery(id+"F0.wireOp",EDGE,"E5.MirrorCS");var subQ1=sQuery(id+"F0.wireOp",EDGE,"E1.sketch_text.stroke-23");var subQ2=makeQuery(id+"F0.imprint","INTERSECT",VERTEX,{"derivedFrom":[subQ1,subQ0]});Q7=makeQuery(id+"F0.imprint","IMPRINT",FACE,{"disambiguationData":[TD([[makeQuery(id+"F0.imprint","IMPRINT",EDGE,{"disambiguationData":[TD([[subQ2,1.0]])],"derivedFrom":subQ1}),-1.0]])]});}
            var Q8;
            {var subQ7=sQuery(id+"F0.wireOp",EDGE,"E1.sketch_text.stroke-23");var subQ8=sQuery(id+"F0.wireOp",EDGE,"E1.sketch_text.stroke-22");var subQ9=makeQuery(id+"F0.imprint","INTERSECT",VERTEX,{"derivedFrom":[subQ8,subQ7]});Q8=makeQuery(id+"F0.imprint","IMPRINT",FACE,{"disambiguationData":[TD([[makeQuery(id+"F0.imprint","IMPRINT",EDGE,{"disambiguationData":[TD([[subQ9,1.0]])],"derivedFrom":subQ8}),-1.0]])]});}
            var Q9;
            {var subQ7=sQuery(id+"F0.wireOp",EDGE,"E1.sketch_text.stroke-20");Q9=makeQuery(id+"F0.imprint","IMPRINT",FACE,{"disambiguationData":[TD([[makeQuery(id+"F0.imprint","IMPRINT",EDGE,{"derivedFrom":subQ7}),-1.0]])]});}
            var Q10;
            {var subQ7=sQuery(id+"F0.wireOp",EDGE,"E1.sketch_text.stroke-26");var subQ8=sQuery(id+"F0.wireOp",EDGE,"E1.sketch_text.stroke-19");var subQ9=makeQuery(id+"F0.imprint","INTERSECT",VERTEX,{"derivedFrom":[subQ8,subQ7]});Q10=makeQuery(id+"F0.imprint","IMPRINT",FACE,{"disambiguationData":[TD([[makeQuery(id+"F0.imprint","IMPRINT",EDGE,{"disambiguationData":[TD([[subQ9,-1.0]])],"derivedFrom":subQ8}),-1.0]])]});}
            var Q11;
            {var subQ0=sQuery(id+"F0.wireOp",EDGE,"E5.MirrorCS");var subQ1=sQuery(id+"F0.wireOp",EDGE,"E1.sketch_text.stroke-26");var subQ2=makeQuery(id+"F0.imprint","INTERSECT",VERTEX,{"derivedFrom":[subQ1,subQ0]});Q11=makeQuery(id+"F0.imprint","IMPRINT",FACE,{"disambiguationData":[TD([[makeQuery(id+"F0.imprint","IMPRINT",EDGE,{"disambiguationData":[TD([[subQ2,-1.0]])],"derivedFrom":subQ1}),-1.0]])]});}
            var Q12;
            {var subQ1=sQuery(id+"F0.wireOp",EDGE,"E1.sketch_text.stroke-36");var subQ5=sQuery(id+"F0.wireOp",EDGE,"E1.sketch_text.stroke-37");var subQ6=makeQuery(id+"F0.imprint","INTERSECT",VERTEX,{"derivedFrom":[subQ1,subQ5]});Q12=makeQuery(id+"F0.imprint","IMPRINT",FACE,{"disambiguationData":[TD([[makeQuery(id+"F0.imprint","IMPRINT",EDGE,{"disambiguationData":[TD([[subQ6,1.0]])],"derivedFrom":subQ1}),-1.0]])]});}
            var Q13;
            {var subQ0=sQuery(id+"F0.wireOp",EDGE,"E5.MirrorCS");var subQ1=sQuery(id+"F0.wireOp",EDGE,"E1.sketch_text.stroke-36");var subQ2=makeQuery(id+"F0.imprint","INTERSECT",VERTEX,{"derivedFrom":[subQ1,subQ0]});Q13=makeQuery(id+"F0.imprint","IMPRINT",FACE,{"disambiguationData":[TD([[makeQuery(id+"F0.imprint","IMPRINT",EDGE,{"disambiguationData":[TD([[subQ2,-1.0]])],"derivedFrom":subQ1}),-1.0]])]});}
            var Q14;
            {var subQ1=sQuery(id+"F0.wireOp",EDGE,"E1.sketch_text.stroke-35");Q14=makeQuery(id+"F0.imprint","IMPRINT",FACE,{"disambiguationData":[TD([[makeQuery(id+"F0.imprint","IMPRINT",EDGE,{"derivedFrom":subQ1}),-1.0]])]});}
            var Q15;
            {var subQ0=sQuery(id+"F0.wireOp",EDGE,"E4.0");var subQ1=sQuery(id+"F0.wireOp",EDGE,"E1.sketch_text.stroke-34");var subQ2=makeQuery(id+"F0.imprint","INTERSECT",VERTEX,{"derivedFrom":[subQ1,subQ0]});Q15=makeQuery(id+"F0.imprint","IMPRINT",FACE,{"disambiguationData":[TD([[makeQuery(id+"F0.imprint","IMPRINT",EDGE,{"disambiguationData":[TD([[subQ2,-1.0]])],"derivedFrom":subQ1}),-1.0]])]});}
            var Q16;
            {var subQ0=sQuery(id+"F0.wireOp",EDGE,"E3");var subQ1=sQuery(id+"F0.wireOp",EDGE,"E1.sketch_text.stroke-34");var subQ2=makeQuery(id+"F0.imprint","INTERSECT",VERTEX,{"derivedFrom":[subQ1,subQ0]});Q16=makeQuery(id+"F0.imprint","IMPRINT",FACE,{"disambiguationData":[TD([[makeQuery(id+"F0.imprint","IMPRINT",EDGE,{"disambiguationData":[TD([[subQ2,-1.0]])],"derivedFrom":subQ1}),-1.0]])]});}
            var Q17;
            {var subQ2=sQuery(id+"F0.wireOp",EDGE,"E1.sketch_text.stroke-33");Q17=makeQuery(id+"F0.imprint","IMPRINT",FACE,{"disambiguationData":[TD([[makeQuery(id+"F0.imprint","IMPRINT",EDGE,{"derivedFrom":subQ2}),-1.0]])]});}
            var Q18;
            {var subQ0=sQuery(id+"F0.wireOp",EDGE,"E1.sketch_text.stroke-38");Q18=makeQuery(id+"F0.imprint","IMPRINT",FACE,{"disambiguationData":[TD([[makeQuery(id+"F0.imprint","IMPRINT",EDGE,{"derivedFrom":subQ0}),-1.0]])]});}
            var Q19;
            {var subQ0=sQuery(id+"F0.wireOp",EDGE,"E1.sketch_text.stroke-45");Q19=makeQuery(id+"F0.imprint","IMPRINT",FACE,{"disambiguationData":[TD([[makeQuery(id+"F0.imprint","IMPRINT",EDGE,{"derivedFrom":subQ0}),-1.0]])]});}
            var Q20;
            {var subQ1=sQuery(id+"F0.wireOp",EDGE,"E1.sketch_text.stroke-43");var subQ5=sQuery(id+"F0.wireOp",EDGE,"E1.sketch_text.stroke-44");var subQ6=makeQuery(id+"F0.imprint","INTERSECT",VERTEX,{"derivedFrom":[subQ1,subQ5]});Q20=makeQuery(id+"F0.imprint","IMPRINT",FACE,{"disambiguationData":[TD([[makeQuery(id+"F0.imprint","IMPRINT",EDGE,{"disambiguationData":[TD([[subQ6,1.0]])],"derivedFrom":subQ1}),-1.0]])]});}
            var Q21;
            {var subQ0=sQuery(id+"F0.wireOp",EDGE,"E4.0");var subQ1=sQuery(id+"F0.wireOp",EDGE,"E1.sketch_text.stroke-43");var subQ2=makeQuery(id+"F0.imprint","INTERSECT",VERTEX,{"derivedFrom":[subQ1,subQ0]});Q21=makeQuery(id+"F0.imprint","IMPRINT",FACE,{"disambiguationData":[TD([[makeQuery(id+"F0.imprint","IMPRINT",EDGE,{"disambiguationData":[TD([[subQ2,-1.0]])],"derivedFrom":subQ1}),-1.0]])]});}
            var Q22;
            {var subQ0=sQuery(id+"F0.wireOp",EDGE,"E1.sketch_text.stroke-54");Q22=makeQuery(id+"F0.imprint","IMPRINT",FACE,{"disambiguationData":[TD([[makeQuery(id+"F0.imprint","IMPRINT",EDGE,{"derivedFrom":subQ0}),-1.0]])]});}
            var Q23;
            {var subQ0=sQuery(id+"F0.wireOp",EDGE,"E1.sketch_text.stroke-48");Q23=makeQuery(id+"F0.imprint","IMPRINT",FACE,{"disambiguationData":[TD([[makeQuery(id+"F0.imprint","IMPRINT",EDGE,{"derivedFrom":subQ0}),-1.0]])]});}
            var Q24;
            {var subQ1=sQuery(id+"F0.wireOp",EDGE,"E1.sketch_text.stroke-50");Q24=makeQuery(id+"F0.imprint","IMPRINT",FACE,{"disambiguationData":[TD([[makeQuery(id+"F0.imprint","IMPRINT",EDGE,{"derivedFrom":subQ1}),-1.0]])]});}
            var Q25;
            {var subQ0=sQuery(id+"F0.wireOp",EDGE,"E3");var subQ1=sQuery(id+"F0.wireOp",EDGE,"E1.sketch_text.stroke-49");var subQ2=makeQuery(id+"F0.imprint","INTERSECT",VERTEX,{"derivedFrom":[subQ1,subQ0]});Q25=makeQuery(id+"F0.imprint","IMPRINT",FACE,{"disambiguationData":[TD([[makeQuery(id+"F0.imprint","IMPRINT",EDGE,{"disambiguationData":[TD([[subQ2,-1.0]])],"derivedFrom":subQ1}),-1.0]])]});}
            var Q26;
            {var subQ0=sQuery(id+"F0.wireOp",EDGE,"E1.sketch_text.stroke-55");var subQ1=sQuery(id+"F0.wireOp",EDGE,"E1.sketch_text.stroke-47");var subQ2=makeQuery(id+"F0.imprint","INTERSECT",VERTEX,{"derivedFrom":[subQ1,subQ0]});Q26=makeQuery(id+"F0.imprint","IMPRINT",FACE,{"disambiguationData":[TD([[makeQuery(id+"F0.imprint","IMPRINT",EDGE,{"disambiguationData":[TD([[subQ2,-1.0]])],"derivedFrom":subQ1}),-1.0]])]});}
            var Q27;
            Q27=makeQuery(id+"F0.imprint","IMPRINT",FACE,{"disambiguationData":[TD([[makeQuery(id+"F0.imprint","IMPRINT",EDGE,{"derivedFrom":sQuery(id+"F0.wireOp",EDGE,"E2.sketch_text.stroke-10")}),-1.0]])]});
            var Q28;
            {var subQ0=sQuery(id+"F0.wireOp",EDGE,"E2.sketch_text.stroke-25");Q28=makeQuery(id+"F0.imprint","IMPRINT",FACE,{"disambiguationData":[TD([[makeQuery(id+"F0.imprint","IMPRINT",EDGE,{"derivedFrom":subQ0}),-1.0]])]});}
            var Q29;
            {var subQ2=sQuery(id+"F0.wireOp",EDGE,"E2.sketch_text.stroke-37");Q29=makeQuery(id+"F0.imprint","IMPRINT",FACE,{"disambiguationData":[TD([[makeQuery(id+"F0.imprint","IMPRINT",EDGE,{"derivedFrom":subQ2}),-1.0]])]});}
            var Q30;
            {var subQ0=sQuery(id+"F0.wireOp",EDGE,"E2.sketch_text.stroke-52");Q30=makeQuery(id+"F0.imprint","IMPRINT",FACE,{"disambiguationData":[TD([[makeQuery(id+"F0.imprint","IMPRINT",EDGE,{"derivedFrom":subQ0}),-1.0]])]});}
            var Q31;
            {var subQ0=sQuery(id+"F0.wireOp",EDGE,"E2.sketch_text.stroke-58");Q31=makeQuery(id+"F0.imprint","IMPRINT",FACE,{"disambiguationData":[TD([[makeQuery(id+"F0.imprint","IMPRINT",EDGE,{"derivedFrom":subQ0}),-1.0]])]});}
            var Q32;
            {var subQ0=sQuery(id+"F0.wireOp",EDGE,"E2.sketch_text.stroke-59");Q32=makeQuery(id+"F0.imprint","IMPRINT",FACE,{"disambiguationData":[TD([[makeQuery(id+"F0.imprint","IMPRINT",EDGE,{"derivedFrom":subQ0}),-1.0]])]});}
            var Q33;
            {var subQ0=sQuery(id+"F0.wireOp",EDGE,"E2.sketch_text.stroke-69");Q33=makeQuery(id+"F0.imprint","IMPRINT",FACE,{"disambiguationData":[TD([[makeQuery(id+"F0.imprint","IMPRINT",EDGE,{"derivedFrom":subQ0}),-1.0]])]});}
            var Q34;
            {var subQ0=sQuery(id+"F0.wireOp",EDGE,"E7.0");var subQ1=sQuery(id+"F0.wireOp",EDGE,"E2.sketch_text.stroke-49");var subQ2=makeQuery(id+"F0.imprint","INTERSECT",VERTEX,{"derivedFrom":[subQ1,subQ0]});Q34=makeQuery(id+"F0.imprint","IMPRINT",FACE,{"disambiguationData":[TD([[makeQuery(id+"F0.imprint","IMPRINT",EDGE,{"disambiguationData":[TD([[subQ2,-1.0]])],"derivedFrom":subQ1}),-1.0]])]});}
            var Q35;
            {var subQ0=sQuery(id+"F0.wireOp",EDGE,"E8.MirrorCS");var subQ1=sQuery(id+"F0.wireOp",EDGE,"E2.sketch_text.stroke-49");var subQ2=makeQuery(id+"F0.imprint","INTERSECT",VERTEX,{"derivedFrom":[subQ1,subQ0]});Q35=makeQuery(id+"F0.imprint","IMPRINT",FACE,{"disambiguationData":[TD([[makeQuery(id+"F0.imprint","IMPRINT",EDGE,{"disambiguationData":[TD([[subQ2,1.0]])],"derivedFrom":subQ1}),-1.0]])]});}
            var Q36;
            {var subQ0=sQuery(id+"F0.wireOp",EDGE,"E2.sketch_text.stroke-50");Q36=makeQuery(id+"F0.imprint","IMPRINT",FACE,{"disambiguationData":[TD([[makeQuery(id+"F0.imprint","IMPRINT",EDGE,{"derivedFrom":subQ0}),-1.0]])]});}
            var Q37;
            {var subQ0=sQuery(id+"F0.wireOp",EDGE,"E2.sketch_text.stroke-56");Q37=makeQuery(id+"F0.imprint","IMPRINT",FACE,{"disambiguationData":[TD([[makeQuery(id+"F0.imprint","IMPRINT",EDGE,{"derivedFrom":subQ0}),-1.0]])]});}
            var Q38;
            {var subQ0=sQuery(id+"F0.wireOp",EDGE,"E8.MirrorCS");var subQ1=sQuery(id+"F0.wireOp",EDGE,"E2.sketch_text.stroke-55");var subQ2=makeQuery(id+"F0.imprint","INTERSECT",VERTEX,{"derivedFrom":[subQ1,subQ0]});Q38=makeQuery(id+"F0.imprint","IMPRINT",FACE,{"disambiguationData":[TD([[makeQuery(id+"F0.imprint","IMPRINT",EDGE,{"disambiguationData":[TD([[subQ2,1.0]])],"derivedFrom":subQ1}),-1.0]])]});}
            var Q39;
            {var subQ0=sQuery(id+"F0.wireOp",EDGE,"E7.0");var subQ1=sQuery(id+"F0.wireOp",EDGE,"E2.sketch_text.stroke-55");var subQ2=makeQuery(id+"F0.imprint","INTERSECT",VERTEX,{"derivedFrom":[subQ1,subQ0]});Q39=makeQuery(id+"F0.imprint","IMPRINT",FACE,{"disambiguationData":[TD([[makeQuery(id+"F0.imprint","IMPRINT",EDGE,{"disambiguationData":[TD([[subQ2,-1.0]])],"derivedFrom":subQ1}),-1.0]])]});}
            var Q40;
            {var subQ1=sQuery(id+"F0.wireOp",EDGE,"E2.sketch_text.stroke-67");Q40=makeQuery(id+"F0.imprint","IMPRINT",FACE,{"disambiguationData":[TD([[makeQuery(id+"F0.imprint","IMPRINT",EDGE,{"derivedFrom":subQ1}),-1.0]])]});}
            var Q41;
            {var subQ1=sQuery(id+"F0.wireOp",EDGE,"E2.sketch_text.stroke-65");Q41=makeQuery(id+"F0.imprint","IMPRINT",FACE,{"disambiguationData":[TD([[makeQuery(id+"F0.imprint","IMPRINT",EDGE,{"derivedFrom":subQ1}),-1.0]])]});}
            var Q42;
            {var subQ1=sQuery(id+"F0.wireOp",EDGE,"E2.sketch_text.stroke-61");Q42=makeQuery(id+"F0.imprint","IMPRINT",FACE,{"disambiguationData":[TD([[makeQuery(id+"F0.imprint","IMPRINT",EDGE,{"derivedFrom":subQ1}),-1.0]])]});}
            var Q43;
            {var subQ5=sQuery(id+"F0.wireOp",EDGE,"E2.sketch_text.stroke-71");Q43=makeQuery(id+"F0.imprint","IMPRINT",FACE,{"disambiguationData":[TD([[makeQuery(id+"F0.imprint","IMPRINT",EDGE,{"derivedFrom":subQ5}),-1.0]])]});}
            var Q44;
            {var subQ0=sQuery(id+"F0.wireOp",EDGE,"E7.0");var subQ1=sQuery(id+"F0.wireOp",EDGE,"E2.sketch_text.stroke-70");var subQ2=makeQuery(id+"F0.imprint","INTERSECT",VERTEX,{"derivedFrom":[subQ1,subQ0]});Q44=makeQuery(id+"F0.imprint","IMPRINT",FACE,{"disambiguationData":[TD([[makeQuery(id+"F0.imprint","IMPRINT",EDGE,{"disambiguationData":[TD([[subQ2,-1.0]])],"derivedFrom":subQ1}),-1.0]])]});}
            var Q45;
            {var subQ0=sQuery(id+"F0.wireOp",EDGE,"E8.MirrorCS");var subQ1=sQuery(id+"F0.wireOp",EDGE,"E2.sketch_text.stroke-70");var subQ2=makeQuery(id+"F0.imprint","INTERSECT",VERTEX,{"derivedFrom":[subQ1,subQ0]});Q45=makeQuery(id+"F0.imprint","IMPRINT",FACE,{"disambiguationData":[TD([[makeQuery(id+"F0.imprint","IMPRINT",EDGE,{"disambiguationData":[TD([[subQ2,1.0]])],"derivedFrom":subQ1}),-1.0]])]});}
            var Q46;
            {var subQ1=sQuery(id+"F0.wireOp",EDGE,"E2.sketch_text.stroke-8");Q46=makeQuery(id+"F0.imprint","IMPRINT",FACE,{"disambiguationData":[TD([[makeQuery(id+"F0.imprint","IMPRINT",EDGE,{"derivedFrom":subQ1}),-1.0]])]});}
            var Q47;
            {var subQ1=sQuery(id+"F0.wireOp",EDGE,"E2.sketch_text.stroke-6");Q47=makeQuery(id+"F0.imprint","IMPRINT",FACE,{"disambiguationData":[TD([[makeQuery(id+"F0.imprint","IMPRINT",EDGE,{"derivedFrom":subQ1}),-1.0]])]});}
            var Q48;
            {var subQ0=sQuery(id+"F0.wireOp",EDGE,"E2.sketch_text.stroke-0");Q48=makeQuery(id+"F0.imprint","IMPRINT",FACE,{"disambiguationData":[TD([[makeQuery(id+"F0.imprint","IMPRINT",EDGE,{"derivedFrom":subQ0}),-1.0]])]});}
            var Q49;
            {var subQ6=sQuery(id+"F0.wireOp",EDGE,"E2.sketch_text.stroke-2");Q49=makeQuery(id+"F0.imprint","IMPRINT",FACE,{"disambiguationData":[TD([[makeQuery(id+"F0.imprint","IMPRINT",EDGE,{"derivedFrom":subQ6}),-1.0]])]});}
            var Q50;
            {var subQ6=sQuery(id+"F0.wireOp",EDGE,"E2.sketch_text.stroke-15");Q50=makeQuery(id+"F0.imprint","IMPRINT",FACE,{"disambiguationData":[TD([[makeQuery(id+"F0.imprint","IMPRINT",EDGE,{"derivedFrom":subQ6}),-1.0]])]});}
            var Q51;
            {var subQ0=sQuery(id+"F0.wireOp",EDGE,"E2.sketch_text.stroke-21");Q51=makeQuery(id+"F0.imprint","IMPRINT",FACE,{"disambiguationData":[TD([[makeQuery(id+"F0.imprint","IMPRINT",EDGE,{"derivedFrom":subQ0}),-1.0]])]});}
            var Q52;
            {var subQ0=sQuery(id+"F0.wireOp",EDGE,"E8.MirrorCS");var subQ1=sQuery(id+"F0.wireOp",EDGE,"E2.sketch_text.stroke-16");var subQ2=makeQuery(id+"F0.imprint","INTERSECT",VERTEX,{"derivedFrom":[subQ1,subQ0]});Q52=makeQuery(id+"F0.imprint","IMPRINT",FACE,{"disambiguationData":[TD([[makeQuery(id+"F0.imprint","IMPRINT",EDGE,{"disambiguationData":[TD([[subQ2,-1.0]])],"derivedFrom":subQ1}),-1.0]])]});}
            var Q53;
            {var subQ0=sQuery(id+"F0.wireOp",EDGE,"E8.MirrorCS");var subQ1=sQuery(id+"F0.wireOp",EDGE,"E2.sketch_text.stroke-14");var subQ2=makeQuery(id+"F0.imprint","INTERSECT",VERTEX,{"derivedFrom":[subQ1,subQ0]});Q53=makeQuery(id+"F0.imprint","IMPRINT",FACE,{"disambiguationData":[TD([[makeQuery(id+"F0.imprint","IMPRINT",EDGE,{"disambiguationData":[TD([[subQ2,1.0]])],"derivedFrom":subQ1}),-1.0]])]});}
            var Q54;
            {var subQ6=sQuery(id+"F0.wireOp",EDGE,"E2.sketch_text.stroke-24");var subQ9=sQuery(id+"F0.wireOp",EDGE,"E2.sketch_text.stroke-23");var subQ10=makeQuery(id+"F0.imprint","INTERSECT",VERTEX,{"derivedFrom":[subQ9,subQ6]});Q54=makeQuery(id+"F0.imprint","IMPRINT",FACE,{"disambiguationData":[TD([[makeQuery(id+"F0.imprint","IMPRINT",EDGE,{"disambiguationData":[TD([[subQ10,1.0]])],"derivedFrom":subQ9}),-1.0]])]});}
            var Q55;
            {var subQ0=sQuery(id+"F0.wireOp",EDGE,"E8.MirrorCS");var subQ1=sQuery(id+"F0.wireOp",EDGE,"E2.sketch_text.stroke-23");var subQ2=makeQuery(id+"F0.imprint","INTERSECT",VERTEX,{"derivedFrom":[subQ1,subQ0]});Q55=makeQuery(id+"F0.imprint","IMPRINT",FACE,{"disambiguationData":[TD([[makeQuery(id+"F0.imprint","IMPRINT",EDGE,{"disambiguationData":[TD([[subQ2,-1.0]])],"derivedFrom":subQ1}),-1.0]])]});}
            var Q56;
            {var subQ5=sQuery(id+"F0.wireOp",EDGE,"E2.sketch_text.stroke-22");Q56=makeQuery(id+"F0.imprint","IMPRINT",FACE,{"disambiguationData":[TD([[makeQuery(id+"F0.imprint","IMPRINT",EDGE,{"derivedFrom":subQ5}),-1.0]])]});}
            var Q57;
            {var subQ1=sQuery(id+"F0.wireOp",EDGE,"E2.sketch_text.stroke-39");Q57=makeQuery(id+"F0.imprint","IMPRINT",FACE,{"disambiguationData":[TD([[makeQuery(id+"F0.imprint","IMPRINT",EDGE,{"derivedFrom":subQ1}),-1.0]])]});}
            var Q58;
            {var subQ1=sQuery(id+"F0.wireOp",EDGE,"E2.sketch_text.stroke-45");Q58=makeQuery(id+"F0.imprint","IMPRINT",FACE,{"disambiguationData":[TD([[makeQuery(id+"F0.imprint","IMPRINT",EDGE,{"derivedFrom":subQ1}),-1.0]])]});}
            var Q59;
            {var subQ1=sQuery(id+"F0.wireOp",EDGE,"E2.sketch_text.stroke-43");Q59=makeQuery(id+"F0.imprint","IMPRINT",FACE,{"disambiguationData":[TD([[makeQuery(id+"F0.imprint","IMPRINT",EDGE,{"derivedFrom":subQ1}),-1.0]])]});}
            extrude(context, id + "F5", {"entities" : qUnion([Q0, Q1, Q2, Q3, Q4, Q5, Q6, Q7, Q8, Q9, Q10, Q11, Q12, Q13, Q14, Q15, Q16, Q17, Q18, Q19, Q20, Q21, Q22, Q23, Q24, Q25, Q26, Q27, Q28, Q29, Q30, Q31, Q32, Q33, Q34, Q35, Q36, Q37, Q38, Q39, Q40, Q41, Q42, Q43, Q44, Q45, Q46, Q47, Q48, Q49, Q50, Q51, Q52, Q53, Q54, Q55, Q56, Q57, Q58, Q59]), "operationType" : NewBodyOperationType.ADD, "depth" : 2 * mm, "offsetDistance" : 25 * mm});
        }
        {
            var Q0;
            Q0=makeQuery(id+"F3.opExtrude","SWEPT_BODY",BODY,{"disambiguationData":[OSD([sQuery(id+"F2.wireOp",EDGE,"E9")])]});
            var Q1;
            Q1=makeQuery(id+"F1.opExtrude","SWEPT_BODY",BODY,{"disambiguationData":[OSD([sQuery(id+"F0.wireOp",EDGE,"E0.sketch_text.stroke-29"),sQuery(id+"F0.wireOp",EDGE,"E0.sketch_text.stroke-30"),sQuery(id+"F0.wireOp",EDGE,"E0.sketch_text.stroke-31"),sQuery(id+"F0.wireOp",EDGE,"E0.sketch_text.stroke-32"),sQuery(id+"F0.wireOp",EDGE,"E0.sketch_text.stroke-33"),sQuery(id+"F0.wireOp",EDGE,"E0.sketch_text.stroke-34"),sQuery(id+"F0.wireOp",EDGE,"E0.sketch_text.stroke-35"),sQuery(id+"F0.wireOp",EDGE,"E0.sketch_text.stroke-36"),sQuery(id+"F0.wireOp",EDGE,"E0.sketch_text.stroke-37"),sQuery(id+"F0.wireOp",EDGE,"E0.sketch_text.stroke-38"),sQuery(id+"F0.wireOp",EDGE,"E0.sketch_text.stroke-39"),sQuery(id+"F0.wireOp",EDGE,"E0.sketch_text.stroke-40"),sQuery(id+"F0.wireOp",EDGE,"E0.sketch_text.stroke-41"),sQuery(id+"F0.wireOp",EDGE,"E0.sketch_text.stroke-42"),sQuery(id+"F0.wireOp",EDGE,"E0.sketch_text.stroke-43")])]});
            var Q2;
            Q2=makeQuery(id+"F1.opExtrude","SWEPT_BODY",BODY,{"disambiguationData":[OSD([sQuery(id+"F0.wireOp",EDGE,"E0.sketch_text.stroke-0"),sQuery(id+"F0.wireOp",EDGE,"E0.sketch_text.stroke-1"),sQuery(id+"F0.wireOp",EDGE,"E0.sketch_text.stroke-2"),sQuery(id+"F0.wireOp",EDGE,"E0.sketch_text.stroke-3"),sQuery(id+"F0.wireOp",EDGE,"E0.sketch_text.stroke-4"),sQuery(id+"F0.wireOp",EDGE,"E0.sketch_text.stroke-5"),sQuery(id+"F0.wireOp",EDGE,"E0.sketch_text.stroke-6"),sQuery(id+"F0.wireOp",EDGE,"E0.sketch_text.stroke-7"),sQuery(id+"F0.wireOp",EDGE,"E0.sketch_text.stroke-8"),sQuery(id+"F0.wireOp",EDGE,"E0.sketch_text.stroke-9"),sQuery(id+"F0.wireOp",EDGE,"E0.sketch_text.stroke-10"),sQuery(id+"F0.wireOp",EDGE,"E0.sketch_text.stroke-11"),sQuery(id+"F0.wireOp",EDGE,"E0.sketch_text.stroke-12"),sQuery(id+"F0.wireOp",EDGE,"E0.sketch_text.stroke-13"),sQuery(id+"F0.wireOp",EDGE,"E0.sketch_text.stroke-14"),sQuery(id+"F0.wireOp",EDGE,"E0.sketch_text.stroke-15"),sQuery(id+"F0.wireOp",EDGE,"E0.sketch_text.stroke-16"),sQuery(id+"F0.wireOp",EDGE,"E0.sketch_text.stroke-17"),sQuery(id+"F0.wireOp",EDGE,"E0.sketch_text.stroke-18"),sQuery(id+"F0.wireOp",EDGE,"E0.sketch_text.stroke-19"),sQuery(id+"F0.wireOp",EDGE,"E0.sketch_text.stroke-20"),sQuery(id+"F0.wireOp",EDGE,"E0.sketch_text.stroke-21"),sQuery(id+"F0.wireOp",EDGE,"E0.sketch_text.stroke-22"),sQuery(id+"F0.wireOp",EDGE,"E0.sketch_text.stroke-23"),sQuery(id+"F0.wireOp",EDGE,"E0.sketch_text.stroke-24"),sQuery(id+"F0.wireOp",EDGE,"E0.sketch_text.stroke-25"),sQuery(id+"F0.wireOp",EDGE,"E0.sketch_text.stroke-26"),sQuery(id+"F0.wireOp",EDGE,"E0.sketch_text.stroke-27"),sQuery(id+"F0.wireOp",EDGE,"E0.sketch_text.stroke-28")])]});
            var Q3;
            Q3=makeQuery(id+"F1.opExtrude","SWEPT_BODY",BODY,{"disambiguationData":[OSD([sQuery(id+"F0.wireOp",EDGE,"E1.sketch_text.stroke-0"),sQuery(id+"F0.wireOp",EDGE,"E1.sketch_text.stroke-1"),sQuery(id+"F0.wireOp",EDGE,"E1.sketch_text.stroke-2"),sQuery(id+"F0.wireOp",EDGE,"E1.sketch_text.stroke-3"),sQuery(id+"F0.wireOp",EDGE,"E1.sketch_text.stroke-4"),sQuery(id+"F0.wireOp",EDGE,"E1.sketch_text.stroke-5"),sQuery(id+"F0.wireOp",EDGE,"E1.sketch_text.stroke-6"),sQuery(id+"F0.wireOp",EDGE,"E1.sketch_text.stroke-7"),sQuery(id+"F0.wireOp",EDGE,"E1.sketch_text.stroke-8"),sQuery(id+"F0.wireOp",EDGE,"E1.sketch_text.stroke-9"),sQuery(id+"F0.wireOp",EDGE,"E1.sketch_text.stroke-10"),sQuery(id+"F0.wireOp",EDGE,"E1.sketch_text.stroke-11"),sQuery(id+"F0.wireOp",EDGE,"E1.sketch_text.stroke-12"),sQuery(id+"F0.wireOp",EDGE,"E1.sketch_text.stroke-13"),sQuery(id+"F0.wireOp",EDGE,"E1.sketch_text.stroke-15"),sQuery(id+"F0.wireOp",EDGE,"E1.sketch_text.stroke-16"),sQuery(id+"F0.wireOp",EDGE,"E1.sketch_text.stroke-17"),sQuery(id+"F0.wireOp",EDGE,"E1.sketch_text.stroke-18"),sQuery(id+"F0.wireOp",EDGE,"E1.sketch_text.stroke-19"),sQuery(id+"F0.wireOp",EDGE,"E1.sketch_text.stroke-20"),sQuery(id+"F0.wireOp",EDGE,"E1.sketch_text.stroke-21"),sQuery(id+"F0.wireOp",EDGE,"E1.sketch_text.stroke-22"),sQuery(id+"F0.wireOp",EDGE,"E1.sketch_text.stroke-23"),sQuery(id+"F0.wireOp",EDGE,"E1.sketch_text.stroke-24"),sQuery(id+"F0.wireOp",EDGE,"E1.sketch_text.stroke-25"),sQuery(id+"F0.wireOp",EDGE,"E1.sketch_text.stroke-26"),sQuery(id+"F0.wireOp",EDGE,"E1.sketch_text.stroke-27"),sQuery(id+"F0.wireOp",EDGE,"E1.sketch_text.stroke-28"),sQuery(id+"F0.wireOp",EDGE,"E1.sketch_text.stroke-29"),sQuery(id+"F0.wireOp",EDGE,"E1.sketch_text.stroke-30"),sQuery(id+"F0.wireOp",EDGE,"E1.sketch_text.stroke-31"),sQuery(id+"F0.wireOp",EDGE,"E1.sketch_text.stroke-32"),sQuery(id+"F0.wireOp",EDGE,"E1.sketch_text.stroke-33"),sQuery(id+"F0.wireOp",EDGE,"E1.sketch_text.stroke-34"),sQuery(id+"F0.wireOp",EDGE,"E1.sketch_text.stroke-35"),sQuery(id+"F0.wireOp",EDGE,"E1.sketch_text.stroke-36"),sQuery(id+"F0.wireOp",EDGE,"E1.sketch_text.stroke-37"),sQuery(id+"F0.wireOp",EDGE,"E1.sketch_text.stroke-38"),sQuery(id+"F0.wireOp",EDGE,"E1.sketch_text.stroke-39"),sQuery(id+"F0.wireOp",EDGE,"E1.sketch_text.stroke-40"),sQuery(id+"F0.wireOp",EDGE,"E1.sketch_text.stroke-41"),sQuery(id+"F0.wireOp",EDGE,"E1.sketch_text.stroke-42"),sQuery(id+"F0.wireOp",EDGE,"E1.sketch_text.stroke-43"),sQuery(id+"F0.wireOp",EDGE,"E1.sketch_text.stroke-44"),sQuery(id+"F0.wireOp",EDGE,"E1.sketch_text.stroke-45"),sQuery(id+"F0.wireOp",EDGE,"E1.sketch_text.stroke-46"),sQuery(id+"F0.wireOp",EDGE,"E1.sketch_text.stroke-47"),sQuery(id+"F0.wireOp",EDGE,"E1.sketch_text.stroke-48"),sQuery(id+"F0.wireOp",EDGE,"E1.sketch_text.stroke-49"),sQuery(id+"F0.wireOp",EDGE,"E1.sketch_text.stroke-50"),sQuery(id+"F0.wireOp",EDGE,"E1.sketch_text.stroke-51"),sQuery(id+"F0.wireOp",EDGE,"E1.sketch_text.stroke-52"),sQuery(id+"F0.wireOp",EDGE,"E1.sketch_text.stroke-53"),sQuery(id+"F0.wireOp",EDGE,"E1.sketch_text.stroke-54"),sQuery(id+"F0.wireOp",EDGE,"E1.sketch_text.stroke-55"),sQuery(id+"F0.wireOp",EDGE,"E4.0"),sQuery(id+"F0.wireOp",EDGE,"E5.MirrorCS")])]});
            var Q4;
            Q4=makeQuery(id+"F1.opExtrude","SWEPT_BODY",BODY,{"disambiguationData":[OSD([sQuery(id+"F0.wireOp",EDGE,"E2.sketch_text.stroke-0"),sQuery(id+"F0.wireOp",EDGE,"E2.sketch_text.stroke-1"),sQuery(id+"F0.wireOp",EDGE,"E2.sketch_text.stroke-2"),sQuery(id+"F0.wireOp",EDGE,"E2.sketch_text.stroke-3"),sQuery(id+"F0.wireOp",EDGE,"E2.sketch_text.stroke-4"),sQuery(id+"F0.wireOp",EDGE,"E2.sketch_text.stroke-5"),sQuery(id+"F0.wireOp",EDGE,"E2.sketch_text.stroke-9"),sQuery(id+"F0.wireOp",EDGE,"E2.sketch_text.stroke-10"),sQuery(id+"F0.wireOp",EDGE,"E2.sketch_text.stroke-11"),sQuery(id+"F0.wireOp",EDGE,"E2.sketch_text.stroke-12"),sQuery(id+"F0.wireOp",EDGE,"E2.sketch_text.stroke-13"),sQuery(id+"F0.wireOp",EDGE,"E2.sketch_text.stroke-14"),sQuery(id+"F0.wireOp",EDGE,"E2.sketch_text.stroke-15"),sQuery(id+"F0.wireOp",EDGE,"E2.sketch_text.stroke-16"),sQuery(id+"F0.wireOp",EDGE,"E2.sketch_text.stroke-17"),sQuery(id+"F0.wireOp",EDGE,"E2.sketch_text.stroke-18"),sQuery(id+"F0.wireOp",EDGE,"E2.sketch_text.stroke-19"),sQuery(id+"F0.wireOp",EDGE,"E2.sketch_text.stroke-20"),sQuery(id+"F0.wireOp",EDGE,"E2.sketch_text.stroke-21"),sQuery(id+"F0.wireOp",EDGE,"E2.sketch_text.stroke-22"),sQuery(id+"F0.wireOp",EDGE,"E2.sketch_text.stroke-23"),sQuery(id+"F0.wireOp",EDGE,"E2.sketch_text.stroke-24"),sQuery(id+"F0.wireOp",EDGE,"E2.sketch_text.stroke-25"),sQuery(id+"F0.wireOp",EDGE,"E2.sketch_text.stroke-26"),sQuery(id+"F0.wireOp",EDGE,"E2.sketch_text.stroke-27"),sQuery(id+"F0.wireOp",EDGE,"E2.sketch_text.stroke-28"),sQuery(id+"F0.wireOp",EDGE,"E2.sketch_text.stroke-29"),sQuery(id+"F0.wireOp",EDGE,"E2.sketch_text.stroke-30"),sQuery(id+"F0.wireOp",EDGE,"E2.sketch_text.stroke-31"),sQuery(id+"F0.wireOp",EDGE,"E2.sketch_text.stroke-32"),sQuery(id+"F0.wireOp",EDGE,"E2.sketch_text.stroke-33"),sQuery(id+"F0.wireOp",EDGE,"E2.sketch_text.stroke-34"),sQuery(id+"F0.wireOp",EDGE,"E2.sketch_text.stroke-35"),sQuery(id+"F0.wireOp",EDGE,"E2.sketch_text.stroke-36"),sQuery(id+"F0.wireOp",EDGE,"E2.sketch_text.stroke-37"),sQuery(id+"F0.wireOp",EDGE,"E2.sketch_text.stroke-38"),sQuery(id+"F0.wireOp",EDGE,"E2.sketch_text.stroke-39"),sQuery(id+"F0.wireOp",EDGE,"E2.sketch_text.stroke-40"),sQuery(id+"F0.wireOp",EDGE,"E2.sketch_text.stroke-41"),sQuery(id+"F0.wireOp",EDGE,"E2.sketch_text.stroke-42"),sQuery(id+"F0.wireOp",EDGE,"E2.sketch_text.stroke-46"),sQuery(id+"F0.wireOp",EDGE,"E2.sketch_text.stroke-47"),sQuery(id+"F0.wireOp",EDGE,"E2.sketch_text.stroke-48"),sQuery(id+"F0.wireOp",EDGE,"E2.sketch_text.stroke-49"),sQuery(id+"F0.wireOp",EDGE,"E2.sketch_text.stroke-50"),sQuery(id+"F0.wireOp",EDGE,"E2.sketch_text.stroke-51"),sQuery(id+"F0.wireOp",EDGE,"E2.sketch_text.stroke-52"),sQuery(id+"F0.wireOp",EDGE,"E2.sketch_text.stroke-53"),sQuery(id+"F0.wireOp",EDGE,"E2.sketch_text.stroke-54"),sQuery(id+"F0.wireOp",EDGE,"E2.sketch_text.stroke-55"),sQuery(id+"F0.wireOp",EDGE,"E2.sketch_text.stroke-56"),sQuery(id+"F0.wireOp",EDGE,"E2.sketch_text.stroke-57"),sQuery(id+"F0.wireOp",EDGE,"E2.sketch_text.stroke-58"),sQuery(id+"F0.wireOp",EDGE,"E2.sketch_text.stroke-59"),sQuery(id+"F0.wireOp",EDGE,"E2.sketch_text.stroke-60"),sQuery(id+"F0.wireOp",EDGE,"E2.sketch_text.stroke-61"),sQuery(id+"F0.wireOp",EDGE,"E2.sketch_text.stroke-62"),sQuery(id+"F0.wireOp",EDGE,"E2.sketch_text.stroke-63"),sQuery(id+"F0.wireOp",EDGE,"E2.sketch_text.stroke-64"),sQuery(id+"F0.wireOp",EDGE,"E2.sketch_text.stroke-68"),sQuery(id+"F0.wireOp",EDGE,"E2.sketch_text.stroke-69"),sQuery(id+"F0.wireOp",EDGE,"E2.sketch_text.stroke-70"),sQuery(id+"F0.wireOp",EDGE,"E2.sketch_text.stroke-71"),sQuery(id+"F0.wireOp",EDGE,"E2.sketch_text.stroke-72"),sQuery(id+"F0.wireOp",EDGE,"E2.sketch_text.stroke-73"),sQuery(id+"F0.wireOp",EDGE,"E2.sketch_text.stroke-74"),sQuery(id+"F0.wireOp",EDGE,"E2.sketch_text.stroke-75"),sQuery(id+"F0.wireOp",EDGE,"E2.sketch_text.stroke-76"),sQuery(id+"F0.wireOp",EDGE,"E7.0"),sQuery(id+"F0.wireOp",EDGE,"E8.MirrorCS")])]});
            booleanBodies(context, id + "F6", {"operationType" : BooleanOperationType.SUBTRACTION, "tools" : qUnion([Q0]), "targets" : qUnion([Q1, Q2, Q3, Q4])});
        }
    });
